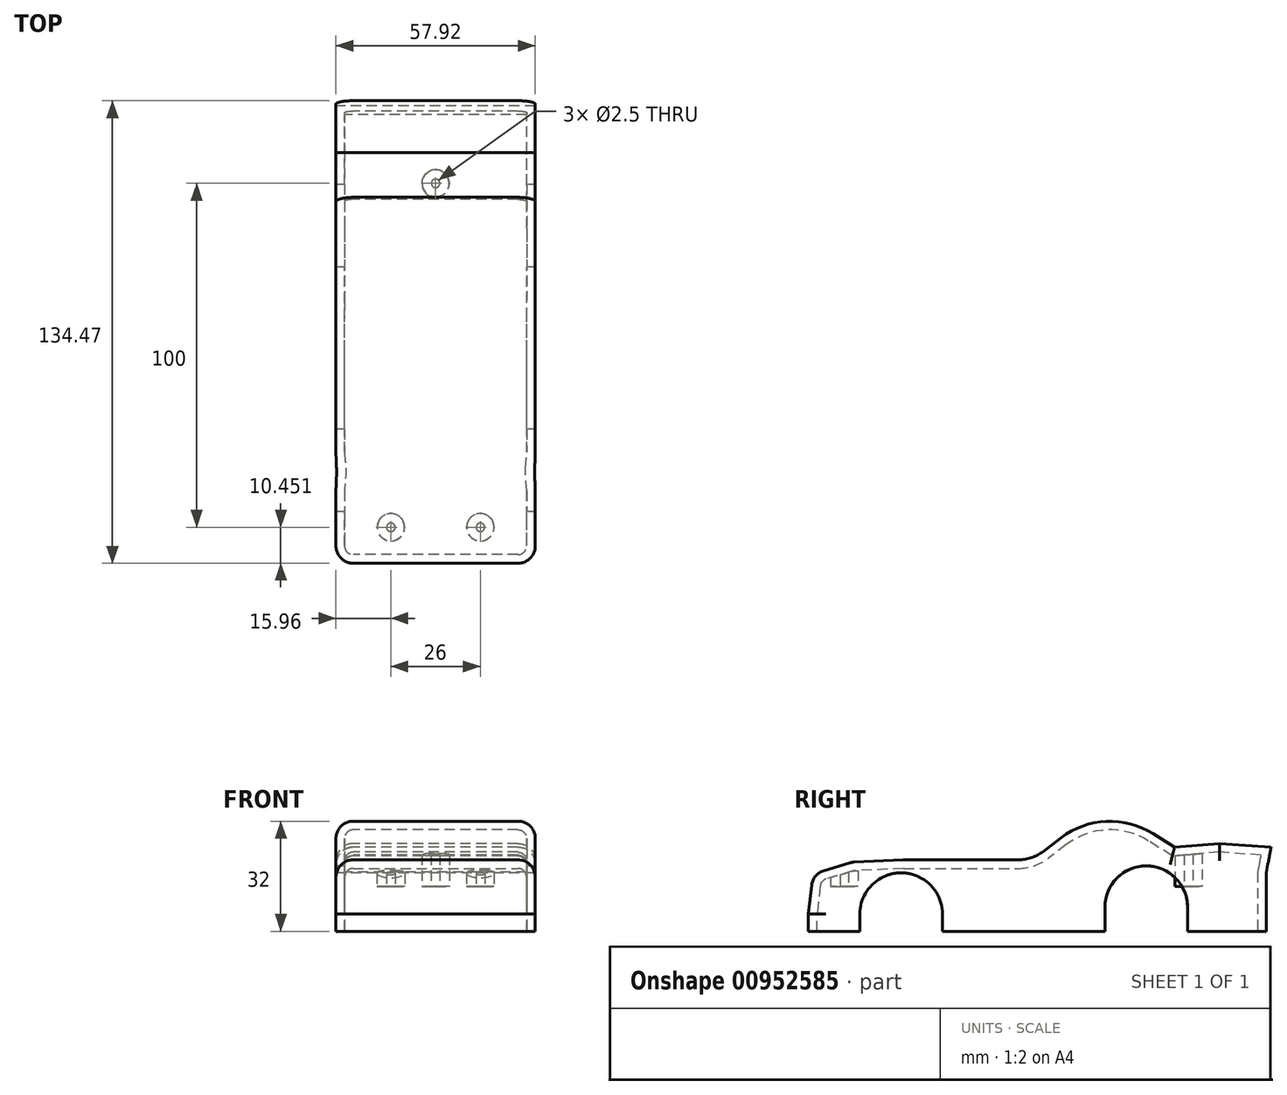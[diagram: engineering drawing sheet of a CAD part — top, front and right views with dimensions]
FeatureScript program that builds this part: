
annotation { "Feature Type Name" : "Feature", "Feature Type Description" : "" }
export const myFeature = defineFeature(function(context is Context, id is Id, definition is map)
    precondition{}
    {
        {
            var Q0;
            Q0=qCreatedBy(makeId("Top.planeOp"),FACE);
            cPlane(context, id + "F0", {"entities" : qUnion([Q0]), "cplaneType" : CPlaneType.OFFSET, "offset" : 8 * mm, "width" : 150 * mm, "height" : 150 * mm});
        }
        {
            var Q0;
            Q0=qCreatedBy(makeId("Right.planeOp"),FACE);
            var sketch = newSketch(context, id + "F1", { "sketchPlane" : qUnion([Q0])});
            skCircle(sketch, "E0", {"center": v(-19.78, 0) * mm, "radius": 12 * mm});
            skCircle(sketch, "E1", {"center": v(51.44, 2) * mm, "radius": 12 * mm});
            skLineSegment(sketch, "E2", {"start": v(-31.78, 0) * mm, "end": v(-46.73, 0) * mm});
            skLineSegment(sketch, "E3", {"start": v(-46.73, 0) * mm, "end": v(-45.78, 8.4) * mm});
            skLineSegment(sketch, "E4", {"start": v(-42.25, 12.63) * mm, "end": v(-34.65, 14.9) * mm});
            skLineSegment(sketch, "E5", {"start": v(-33.44, 15.1) * mm, "end": v(-19.1, 15.76) * mm});
            skLineSegment(sketch, "E6", {"start": v(-19.1, 15.76) * mm, "end": v(14.17, 15.76) * mm});
            skLineSegment(sketch, "E7", {"start": v(21.52, 18.24) * mm, "end": v(26.7, 22.19) * mm});
            skLineSegment(sketch, "E8", {"start": v(53.4, 23.42) * mm, "end": v(59.66, 19.5) * mm});
            skLineSegment(sketch, "E9", {"start": v(59.66, 19.5) * mm, "end": v(72.69, 20.52) * mm});
            skLineSegment(sketch, "E10", {"start": v(86.27, 11.94) * mm, "end": v(86.27, 0) * mm});
            skLineSegment(sketch, "E11", {"start": v(86.27, 0) * mm, "end": v(63.27, 0) * mm});
            skLineSegment(sketch, "E12", {"start": v(-7.78, 0) * mm, "end": v(39.6, 0) * mm});
            skPoint(sketch, "E13.visualSharp", {"position": v(-45.4, 11.68) * mm});
            skPoint(sketch, "E14.visualSharp", {"position": v(-34.06, 15.08) * mm});
            skArc(sketch, "E14.filletArc", {"start": v(-33.44, 15.1) * mm, "mid": v(-34.05, 15.04) * mm, "end": v(-34.65, 14.9) * mm});
            skPoint(sketch, "E15.visualSharp", {"position": v(-19.1, 15.76) * mm});
            skPoint(sketch, "E16.visualSharp", {"position": v(18.27, 15.76) * mm});
            skArc(sketch, "E16.filletArc", {"start": v(14.17, 15.76) * mm, "mid": v(18.05, 16.4) * mm, "end": v(21.52, 18.24) * mm});
            skPoint(sketch, "E17.visualSharp", {"position": v(39.62, 32.05) * mm});
            skArc(sketch, "E17.filletArc", {"start": v(53.4, 23.42) * mm, "mid": v(39.85, 26.97) * mm, "end": v(26.7, 22.19) * mm});
            skPoint(sketch, "E18.visualSharp", {"position": v(59.66, 19.5) * mm});
            skPoint(sketch, "E19.visualSharp", {"position": v(86.27, 21.57) * mm});
            skLineSegment(sketch, "E20", {"start": v(72.69, 20.52) * mm, "end": v(87.74, 19.46) * mm});
            skLineSegment(sketch, "E21", {"start": v(87.74, 19.46) * mm, "end": v(86.27, 11.94) * mm});
            skLineSegment(sketch, "E22", {"start": v(-31.78, 0) * mm, "end": v(-7.78, 0) * mm});
            skLineSegment(sketch, "E23", {"start": v(39.6, 0) * mm, "end": v(63.27, 0) * mm});
            skLineSegment(sketch, "E24", {"start": v(63.44, 2) * mm, "end": v(63.44, 0) * mm});
            skLineSegment(sketch, "E25", {"start": v(39.44, 2) * mm, "end": v(39.44, 0) * mm});
            skArc(sketch, "E26.filletArc", {"start": v(-42.25, 12.63) * mm, "mid": v(-44.65, 11.04) * mm, "end": v(-45.78, 8.4) * mm});
            skSolve(sketch);
        }
        {
            var Q0;
            Q0=qCreatedBy(id+"F0.planeOp",FACE);
            var sketch = newSketch(context, id + "F2", { "sketchPlane" : qUnion([Q0])});
            skLineSegment(sketch, "E27", {"start": v(0, -36.28) * mm, "end": v(0, 63.72) * mm, "construction": true});
            skLineSegment(sketch, "E28", {"start": v(0, -36.28) * mm, "end": v(13, -36.28) * mm, "construction": true});
            skLineSegment(sketch, "E29.MirrorCS", {"start": v(0, -36.28) * mm, "end": v(-13, -36.28) * mm, "construction": true});
            skCircle(sketch, "E30", {"center": v(13, -36.28) * mm, "radius": 4 * mm});
            skCircle(sketch, "E31", {"center": v(-13, -36.28) * mm, "radius": 4 * mm});
            skCircle(sketch, "E32", {"center": v(0, 63.72) * mm, "radius": 4 * mm});
            skCircle(sketch, "E33", {"center": v(-13, -36.28) * mm, "radius": 1.25 * mm});
            skCircle(sketch, "E34", {"center": v(13, -36.28) * mm, "radius": 1.25 * mm});
            skCircle(sketch, "E35", {"center": v(0, 63.72) * mm, "radius": 1.25 * mm});
            skSolve(sketch);
        }
        {
            var Q0;
            {var subQ1=sQuery(id+"F1.wireOp",EDGE,"E2");Q0=makeQuery(id+"F1.imprint","IMPRINT",FACE,{"disambiguationData":[TD([[makeQuery(id+"F1.imprint","IMPRINT",EDGE,{"derivedFrom":subQ1}),-1.0]])]});}
            var Q1;
            {var subQ0=sQuery(id+"F1.wireOp",EDGE,"E23");Q1=makeQuery(id+"F1.imprint","IMPRINT",FACE,{"disambiguationData":[TD([[makeQuery(id+"F1.imprint","IMPRINT",EDGE,{"derivedFrom":subQ0}),1.0]])]});}
            var Q2;
            {var subQ3=sQuery(id+"F1.wireOp",EDGE,"E25");Q2=makeQuery(id+"F1.imprint","IMPRINT",FACE,{"disambiguationData":[TD([[makeQuery(id+"F1.imprint","IMPRINT",EDGE,{"derivedFrom":subQ3}),1.0]])]});}
            var Q3;
            {var subQ3=sQuery(id+"F1.wireOp",EDGE,"E24");Q3=makeQuery(id+"F1.imprint","IMPRINT",FACE,{"disambiguationData":[TD([[makeQuery(id+"F1.imprint","IMPRINT",EDGE,{"derivedFrom":subQ3}),-1.0]])]});}
            var Q4;
            {var subQ0=sQuery(id+"F1.wireOp",EDGE,"E22");Q4=makeQuery(id+"F1.imprint","IMPRINT",FACE,{"disambiguationData":[TD([[makeQuery(id+"F1.imprint","IMPRINT",EDGE,{"derivedFrom":subQ0}),1.0]])]});}
            extrude(context, id + "F3", {"entities" : qUnion([Q0, Q1, Q2, Q3, Q4]), "depth" : 57.9 * mm, "symmetric" : true});
        }
        {
            var Q0;
            Q0=makeQuery(id+"F3.opExtrude","CAP_EDGE",EDGE,{"disambiguationData":[OSD([sQuery(id+"F1.wireOp",EDGE,"E3")])],"isStart":false});
            var Q1;
            Q1=makeQuery(id+"F3.opExtrude","CAP_EDGE",EDGE,{"disambiguationData":[OSD([sQuery(id+"F1.wireOp",EDGE,"E4")])],"isStart":false});
            var Q2;
            Q2=makeQuery(id+"F3.opExtrude","CAP_EDGE",EDGE,{"disambiguationData":[OSD([sQuery(id+"F1.wireOp",EDGE,"E6")])],"isStart":false});
            var Q3;
            Q3=makeQuery(id+"F3.opExtrude","CAP_EDGE",EDGE,{"disambiguationData":[OSD([sQuery(id+"F1.wireOp",EDGE,"E5")])],"isStart":false});
            var Q4;
            Q4=makeQuery(id+"F3.opExtrude","CAP_EDGE",EDGE,{"disambiguationData":[OSD([sQuery(id+"F1.wireOp",EDGE,"E14.filletArc")])],"isStart":false});
            var Q5;
            Q5=makeQuery(id+"F3.opExtrude","CAP_EDGE",EDGE,{"disambiguationData":[OSD([sQuery(id+"F1.wireOp",EDGE,"E9")])],"isStart":false});
            var Q6;
            Q6=makeQuery(id+"F3.opExtrude","CAP_EDGE",EDGE,{"disambiguationData":[OSD([sQuery(id+"F1.wireOp",EDGE,"E20")])],"isStart":false});
            var Q7;
            Q7=makeQuery(id+"F3.opExtrude","CAP_EDGE",EDGE,{"disambiguationData":[OSD([sQuery(id+"F1.wireOp",EDGE,"E20")])],"isStart":true});
            var Q8;
            Q8=makeQuery(id+"F3.opExtrude","CAP_EDGE",EDGE,{"disambiguationData":[OSD([sQuery(id+"F1.wireOp",EDGE,"E9")])],"isStart":true});
            var Q9;
            Q9=makeQuery(id+"F3.opExtrude","CAP_EDGE",EDGE,{"disambiguationData":[OSD([sQuery(id+"F1.wireOp",EDGE,"E8")])],"isStart":true});
            var Q10;
            Q10=makeQuery(id+"F3.opExtrude","CAP_EDGE",EDGE,{"disambiguationData":[OSD([sQuery(id+"F1.wireOp",EDGE,"E4")])],"isStart":true});
            var Q11;
            Q11=makeQuery(id+"F3.opExtrude","CAP_EDGE",EDGE,{"disambiguationData":[OSD([sQuery(id+"F1.wireOp",EDGE,"E26.filletArc")])],"isStart":false});
            var Q12;
            Q12=makeQuery(id+"F3.opExtrude","CAP_EDGE",EDGE,{"disambiguationData":[OSD([sQuery(id+"F1.wireOp",EDGE,"E26.filletArc")])],"isStart":true});
            var Q13;
            Q13=makeQuery(id+"F3.opExtrude","CAP_EDGE",EDGE,{"disambiguationData":[OSD([sQuery(id+"F1.wireOp",EDGE,"E3")])],"isStart":true});
            var Q14;
            Q14=makeQuery(id+"F3.opExtrude","CAP_EDGE",EDGE,{"disambiguationData":[OSD([sQuery(id+"F1.wireOp",EDGE,"E5")])],"isStart":true});
            var Q15;
            Q15=makeQuery(id+"F3.opExtrude","SWEPT_EDGE",EDGE,{"disambiguationData":[OSD([sQuery(id+"F1.wireOp",EDGE,"E5"),sQuery(id+"F1.wireOp",EDGE,"E6")])]});
            var Q16;
            Q16=makeQuery(id+"F3.opExtrude","SWEPT_EDGE",EDGE,{"disambiguationData":[OSD([sQuery(id+"F1.wireOp",EDGE,"E4"),sQuery(id+"F1.wireOp",EDGE,"E26.filletArc")])]});
            fillet(context, id + "F4", {"entities" : qUnion([Q0, Q1, Q2, Q3, Q4, Q5, Q6, Q7, Q8, Q9, Q10, Q11, Q12, Q13, Q14, Q15, Q16]), "radius" : 5 * mm, "tangentPropagation" : true, "allowEdgeOverflow" : false});
        }
        {
            var Q0;
            Q0=makeQuery(id+"F3.opExtrude","SWEPT_FACE",FACE,{"disambiguationData":[OSD([sQuery(id+"F1.wireOp",EDGE,"E2"),sQuery(id+"F1.wireOp",EDGE,"E11"),sQuery(id+"F1.wireOp",EDGE,"E12"),sQuery(id+"F1.wireOp",EDGE,"E22"),sQuery(id+"F1.wireOp",EDGE,"E23")])]});
            shell(context, id + "F5", {"entities" : qUnion([Q0]), "thickness" : 2.5 * mm});
        }
        {
            var Q0;
            {var subQ0=sQuery(id+"F1.wireOp",EDGE,"E22");Q0=makeQuery(id+"F1.imprint","IMPRINT",FACE,{"disambiguationData":[TD([[makeQuery(id+"F1.imprint","IMPRINT",EDGE,{"derivedFrom":subQ0}),1.0]])]});}
            var Q1;
            {var subQ0=sQuery(id+"F1.wireOp",EDGE,"E23");Q1=makeQuery(id+"F1.imprint","IMPRINT",FACE,{"disambiguationData":[TD([[makeQuery(id+"F1.imprint","IMPRINT",EDGE,{"derivedFrom":subQ0}),1.0]])]});}
            var Q2;
            {var subQ3=sQuery(id+"F1.wireOp",EDGE,"E25");Q2=makeQuery(id+"F1.imprint","IMPRINT",FACE,{"disambiguationData":[TD([[makeQuery(id+"F1.imprint","IMPRINT",EDGE,{"derivedFrom":subQ3}),1.0]])]});}
            var Q3;
            {var subQ3=sQuery(id+"F1.wireOp",EDGE,"E24");Q3=makeQuery(id+"F1.imprint","IMPRINT",FACE,{"disambiguationData":[TD([[makeQuery(id+"F1.imprint","IMPRINT",EDGE,{"derivedFrom":subQ3}),-1.0]])]});}
            extrude(context, id + "F6", {"entities" : qUnion([Q0, Q1, Q2, Q3]), "operationType" : NewBodyOperationType.REMOVE, "depth" : 60 * mm, "hasSecondDirection" : true, "secondDirectionBound" : BoundingType.THROUGH_ALL, "secondDirectionOppositeDirection" : true, "secondDirectionDepth" : 25 * mm, "symmetric" : true});
        }
        {
            var Q0;
            Q0=qSketchRegion(id+"F2",true);
            var Q1;
            Q1=makeQuery(id+"F3.opExtrude","SWEPT_BODY",BODY,{"disambiguationData":[OSD([sQuery(id+"F1.wireOp",EDGE,"E2"),sQuery(id+"F1.wireOp",EDGE,"E3"),sQuery(id+"F1.wireOp",EDGE,"E4"),sQuery(id+"F1.wireOp",EDGE,"E5"),sQuery(id+"F1.wireOp",EDGE,"E6"),sQuery(id+"F1.wireOp",EDGE,"E7"),sQuery(id+"F1.wireOp",EDGE,"E8"),sQuery(id+"F1.wireOp",EDGE,"E9"),sQuery(id+"F1.wireOp",EDGE,"E10"),sQuery(id+"F1.wireOp",EDGE,"E11"),sQuery(id+"F1.wireOp",EDGE,"E12"),sQuery(id+"F1.wireOp",EDGE,"E14.filletArc"),sQuery(id+"F1.wireOp",EDGE,"E16.filletArc"),sQuery(id+"F1.wireOp",EDGE,"E17.filletArc"),sQuery(id+"F1.wireOp",EDGE,"E20"),sQuery(id+"F1.wireOp",EDGE,"E21"),sQuery(id+"F1.wireOp",EDGE,"E22"),sQuery(id+"F1.wireOp",EDGE,"E23"),sQuery(id+"F1.wireOp",EDGE,"E26.filletArc")])]});
            extrude(context, id + "F7", {"entities" : qUnion([Q0]), "operationType" : NewBodyOperationType.ADD, "endBound" : BoundingType.UP_TO_BODY, "endBoundEntityBody" : qUnion([Q1]), "depth" : 25 * mm});
        }
        {
            var Q0;
            {var subQ0=sQuery(id+"F1.wireOp",EDGE,"E3");var subQ1=makeQuery(id+"F4.opFillet","BLEND_FACE",FACE,{"disambiguationData":[OSD([subQ0]),TDD([makeQuery(id+"F3.opExtrude","CAP_EDGE",EDGE,{"disambiguationData":[OSD([subQ0])],"isStart":false})])]});var subQ2=makeQuery(id+"F3.opExtrude","SWEPT_FACE",FACE,{"disambiguationData":[OSD([subQ0])]});var subQ3=sQuery(id+"F1.wireOp",EDGE,"E26.filletArc");var subQ4=sQuery(id+"F1.wireOp",EDGE,"E23");var subQ5=sQuery(id+"F1.wireOp",EDGE,"E22");var subQ6=sQuery(id+"F1.wireOp",EDGE,"E21");var subQ7=sQuery(id+"F1.wireOp",EDGE,"E20");var subQ8=sQuery(id+"F1.wireOp",EDGE,"E17.filletArc");var subQ9=sQuery(id+"F1.wireOp",EDGE,"E16.filletArc");var subQ10=sQuery(id+"F1.wireOp",EDGE,"E14.filletArc");var subQ11=sQuery(id+"F1.wireOp",EDGE,"E12");var subQ12=sQuery(id+"F1.wireOp",EDGE,"E11");var subQ13=sQuery(id+"F1.wireOp",EDGE,"E10");var subQ14=sQuery(id+"F1.wireOp",EDGE,"E9");var subQ15=sQuery(id+"F1.wireOp",EDGE,"E8");var subQ16=sQuery(id+"F1.wireOp",EDGE,"E7");var subQ17=sQuery(id+"F1.wireOp",EDGE,"E6");var subQ18=sQuery(id+"F1.wireOp",EDGE,"E5");var subQ19=sQuery(id+"F1.wireOp",EDGE,"E4");var subQ20=sQuery(id+"F1.wireOp",EDGE,"E2");var subQ21=makeQuery(id+"F3.opExtrude","CAP_FACE",FACE,{"disambiguationData":[OSD([subQ20,subQ0,subQ19,subQ18,subQ17,subQ16,subQ15,subQ14,subQ13,subQ12,subQ11,subQ10,subQ9,subQ8,subQ7,subQ6,subQ5,subQ4,subQ3])],"isStart":false});var subQ22=makeQuery(id+"F4.opFillet","BLEND_FACE",FACE,{"disambiguationData":[OSD([subQ0]),TDD([makeQuery(id+"F3.opExtrude","CAP_EDGE",EDGE,{"disambiguationData":[OSD([subQ0])],"isStart":true})])]});var subQ23=makeQuery(id+"F3.opExtrude","CAP_FACE",FACE,{"disambiguationData":[OSD([subQ20,subQ0,subQ19,subQ18,subQ17,subQ16,subQ15,subQ14,subQ13,subQ12,subQ11,subQ10,subQ9,subQ8,subQ7,subQ6,subQ5,subQ4,subQ3])],"isStart":true});Q0=makeQuery(id+"F6.boolean.opBoolean","SPLIT",FACE,{"disambiguationData":[TD([subQ23,subQ21,subQ2,subQ22,subQ1,makeQuery(id+"F5.opShell","OFFSET_FACE",FACE,{"disambiguationData":[OSD([subQ0]),TDD([subQ22])]}),makeQuery(id+"F5.opShell","OFFSET_FACE",FACE,{"disambiguationData":[OSD([subQ0]),TDD([subQ1])]}),makeQuery(id+"F5.opShell","OFFSET_FACE",FACE,{"disambiguationData":[OSD([subQ20,subQ0,subQ19,subQ18,subQ17,subQ16,subQ15,subQ14,subQ13,subQ12,subQ11,subQ10,subQ9,subQ8,subQ7,subQ6,subQ5,subQ4,subQ3]),TDD([subQ23])]}),makeQuery(id+"F5.opShell","OFFSET_FACE",FACE,{"disambiguationData":[OSD([subQ20,subQ0,subQ19,subQ18,subQ17,subQ16,subQ15,subQ14,subQ13,subQ12,subQ11,subQ10,subQ9,subQ8,subQ7,subQ6,subQ5,subQ4,subQ3]),TDD([subQ21])]}),makeQuery(id+"F5.opShell","OFFSET_FACE",FACE,{"disambiguationData":[OSD([subQ0]),TDD([subQ2])]}),makeQuery(id+"F6.opExtrude","SWEPT_FACE",FACE,{"disambiguationData":[OSD([sQuery(id+"F1.wireOp",EDGE,"E0")])]})])],"derivedFrom":makeQuery(id+"F3.opExtrude","SWEPT_FACE",FACE,{"disambiguationData":[OSD([subQ20,subQ12,subQ11,subQ5,subQ4])]})});}
            var Q1;
            {var subQ0=sQuery(id+"F1.wireOp",EDGE,"E26.filletArc");var subQ1=sQuery(id+"F1.wireOp",EDGE,"E23");var subQ2=sQuery(id+"F1.wireOp",EDGE,"E22");var subQ3=sQuery(id+"F1.wireOp",EDGE,"E21");var subQ4=sQuery(id+"F1.wireOp",EDGE,"E20");var subQ5=sQuery(id+"F1.wireOp",EDGE,"E17.filletArc");var subQ6=sQuery(id+"F1.wireOp",EDGE,"E16.filletArc");var subQ7=sQuery(id+"F1.wireOp",EDGE,"E14.filletArc");var subQ8=sQuery(id+"F1.wireOp",EDGE,"E12");var subQ9=sQuery(id+"F1.wireOp",EDGE,"E11");var subQ10=sQuery(id+"F1.wireOp",EDGE,"E10");var subQ11=sQuery(id+"F1.wireOp",EDGE,"E9");var subQ12=sQuery(id+"F1.wireOp",EDGE,"E8");var subQ13=sQuery(id+"F1.wireOp",EDGE,"E7");var subQ14=sQuery(id+"F1.wireOp",EDGE,"E6");var subQ15=sQuery(id+"F1.wireOp",EDGE,"E5");var subQ16=sQuery(id+"F1.wireOp",EDGE,"E4");var subQ17=sQuery(id+"F1.wireOp",EDGE,"E3");var subQ18=sQuery(id+"F1.wireOp",EDGE,"E2");var subQ19=makeQuery(id+"F3.opExtrude","CAP_FACE",FACE,{"disambiguationData":[OSD([subQ18,subQ17,subQ16,subQ15,subQ14,subQ13,subQ12,subQ11,subQ10,subQ9,subQ8,subQ7,subQ6,subQ5,subQ4,subQ3,subQ2,subQ1,subQ0])],"isStart":true});Q1=makeQuery(id+"F6.boolean.opBoolean","SPLIT",FACE,{"disambiguationData":[TD([subQ19,makeQuery(id+"F5.opShell","OFFSET_FACE",FACE,{"disambiguationData":[OSD([subQ18,subQ17,subQ16,subQ15,subQ14,subQ13,subQ12,subQ11,subQ10,subQ9,subQ8,subQ7,subQ6,subQ5,subQ4,subQ3,subQ2,subQ1,subQ0]),TDD([subQ19])]}),makeQuery(id+"F6.opExtrude","SWEPT_FACE",FACE,{"disambiguationData":[OSD([sQuery(id+"F1.wireOp",EDGE,"E0")])]}),makeQuery(id+"F6.opExtrude","SWEPT_FACE",FACE,{"disambiguationData":[OSD([sQuery(id+"F1.wireOp",EDGE,"E25")])]})])],"derivedFrom":makeQuery(id+"F3.opExtrude","SWEPT_FACE",FACE,{"disambiguationData":[OSD([subQ18,subQ9,subQ8,subQ2,subQ1])]})});}
            var Q2;
            {var subQ0=sQuery(id+"F1.wireOp",EDGE,"E26.filletArc");var subQ1=sQuery(id+"F1.wireOp",EDGE,"E23");var subQ2=sQuery(id+"F1.wireOp",EDGE,"E22");var subQ3=sQuery(id+"F1.wireOp",EDGE,"E21");var subQ4=sQuery(id+"F1.wireOp",EDGE,"E20");var subQ5=sQuery(id+"F1.wireOp",EDGE,"E17.filletArc");var subQ6=sQuery(id+"F1.wireOp",EDGE,"E16.filletArc");var subQ7=sQuery(id+"F1.wireOp",EDGE,"E14.filletArc");var subQ8=sQuery(id+"F1.wireOp",EDGE,"E12");var subQ9=sQuery(id+"F1.wireOp",EDGE,"E11");var subQ10=sQuery(id+"F1.wireOp",EDGE,"E10");var subQ11=sQuery(id+"F1.wireOp",EDGE,"E9");var subQ12=sQuery(id+"F1.wireOp",EDGE,"E8");var subQ13=sQuery(id+"F1.wireOp",EDGE,"E7");var subQ14=sQuery(id+"F1.wireOp",EDGE,"E6");var subQ15=sQuery(id+"F1.wireOp",EDGE,"E5");var subQ16=sQuery(id+"F1.wireOp",EDGE,"E4");var subQ17=sQuery(id+"F1.wireOp",EDGE,"E3");var subQ18=sQuery(id+"F1.wireOp",EDGE,"E2");var subQ19=makeQuery(id+"F3.opExtrude","CAP_FACE",FACE,{"disambiguationData":[OSD([subQ18,subQ17,subQ16,subQ15,subQ14,subQ13,subQ12,subQ11,subQ10,subQ9,subQ8,subQ7,subQ6,subQ5,subQ4,subQ3,subQ2,subQ1,subQ0])],"isStart":false});Q2=makeQuery(id+"F6.boolean.opBoolean","SPLIT",FACE,{"disambiguationData":[TD([subQ19,makeQuery(id+"F5.opShell","OFFSET_FACE",FACE,{"disambiguationData":[OSD([subQ18,subQ17,subQ16,subQ15,subQ14,subQ13,subQ12,subQ11,subQ10,subQ9,subQ8,subQ7,subQ6,subQ5,subQ4,subQ3,subQ2,subQ1,subQ0]),TDD([subQ19])]}),makeQuery(id+"F6.opExtrude","SWEPT_FACE",FACE,{"disambiguationData":[OSD([sQuery(id+"F1.wireOp",EDGE,"E0")])]}),makeQuery(id+"F6.opExtrude","SWEPT_FACE",FACE,{"disambiguationData":[OSD([sQuery(id+"F1.wireOp",EDGE,"E25")])]})])],"derivedFrom":makeQuery(id+"F3.opExtrude","SWEPT_FACE",FACE,{"disambiguationData":[OSD([subQ18,subQ9,subQ8,subQ2,subQ1])]})});}
            var Q3;
            {var subQ0=sQuery(id+"F1.wireOp",EDGE,"E10");var subQ1=sQuery(id+"F1.wireOp",EDGE,"E26.filletArc");var subQ2=sQuery(id+"F1.wireOp",EDGE,"E23");var subQ3=sQuery(id+"F1.wireOp",EDGE,"E22");var subQ4=sQuery(id+"F1.wireOp",EDGE,"E21");var subQ5=sQuery(id+"F1.wireOp",EDGE,"E20");var subQ6=sQuery(id+"F1.wireOp",EDGE,"E17.filletArc");var subQ7=sQuery(id+"F1.wireOp",EDGE,"E16.filletArc");var subQ8=sQuery(id+"F1.wireOp",EDGE,"E14.filletArc");var subQ9=sQuery(id+"F1.wireOp",EDGE,"E12");var subQ10=sQuery(id+"F1.wireOp",EDGE,"E11");var subQ11=sQuery(id+"F1.wireOp",EDGE,"E9");var subQ12=sQuery(id+"F1.wireOp",EDGE,"E8");var subQ13=sQuery(id+"F1.wireOp",EDGE,"E7");var subQ14=sQuery(id+"F1.wireOp",EDGE,"E6");var subQ15=sQuery(id+"F1.wireOp",EDGE,"E5");var subQ16=sQuery(id+"F1.wireOp",EDGE,"E4");var subQ17=sQuery(id+"F1.wireOp",EDGE,"E3");var subQ18=sQuery(id+"F1.wireOp",EDGE,"E2");var subQ19=makeQuery(id+"F3.opExtrude","CAP_FACE",FACE,{"disambiguationData":[OSD([subQ18,subQ17,subQ16,subQ15,subQ14,subQ13,subQ12,subQ11,subQ0,subQ10,subQ9,subQ8,subQ7,subQ6,subQ5,subQ4,subQ3,subQ2,subQ1])],"isStart":false});var subQ20=makeQuery(id+"F3.opExtrude","CAP_FACE",FACE,{"disambiguationData":[OSD([subQ18,subQ17,subQ16,subQ15,subQ14,subQ13,subQ12,subQ11,subQ0,subQ10,subQ9,subQ8,subQ7,subQ6,subQ5,subQ4,subQ3,subQ2,subQ1])],"isStart":true});Q3=makeQuery(id+"F6.boolean.opBoolean","SPLIT",FACE,{"disambiguationData":[TD([subQ20,subQ19,makeQuery(id+"F3.opExtrude","SWEPT_FACE",FACE,{"disambiguationData":[OSD([subQ0])]}),makeQuery(id+"F5.opShell","OFFSET_FACE",FACE,{"disambiguationData":[OSD([subQ0])]}),makeQuery(id+"F5.opShell","OFFSET_FACE",FACE,{"disambiguationData":[OSD([subQ18,subQ17,subQ16,subQ15,subQ14,subQ13,subQ12,subQ11,subQ0,subQ10,subQ9,subQ8,subQ7,subQ6,subQ5,subQ4,subQ3,subQ2,subQ1]),TDD([subQ20])]}),makeQuery(id+"F5.opShell","OFFSET_FACE",FACE,{"disambiguationData":[OSD([subQ18,subQ17,subQ16,subQ15,subQ14,subQ13,subQ12,subQ11,subQ0,subQ10,subQ9,subQ8,subQ7,subQ6,subQ5,subQ4,subQ3,subQ2,subQ1]),TDD([subQ19])]}),makeQuery(id+"F6.opExtrude","SWEPT_FACE",FACE,{"disambiguationData":[OSD([sQuery(id+"F1.wireOp",EDGE,"E24")])]})])],"derivedFrom":makeQuery(id+"F3.opExtrude","SWEPT_FACE",FACE,{"disambiguationData":[OSD([subQ18,subQ10,subQ9,subQ3,subQ2])]})});}
            extrude(context, id + "F8", {"entities" : qUnion([Q0, Q1, Q2, Q3]), "operationType" : NewBodyOperationType.ADD, "depth" : 5 * mm});
        }
    });
